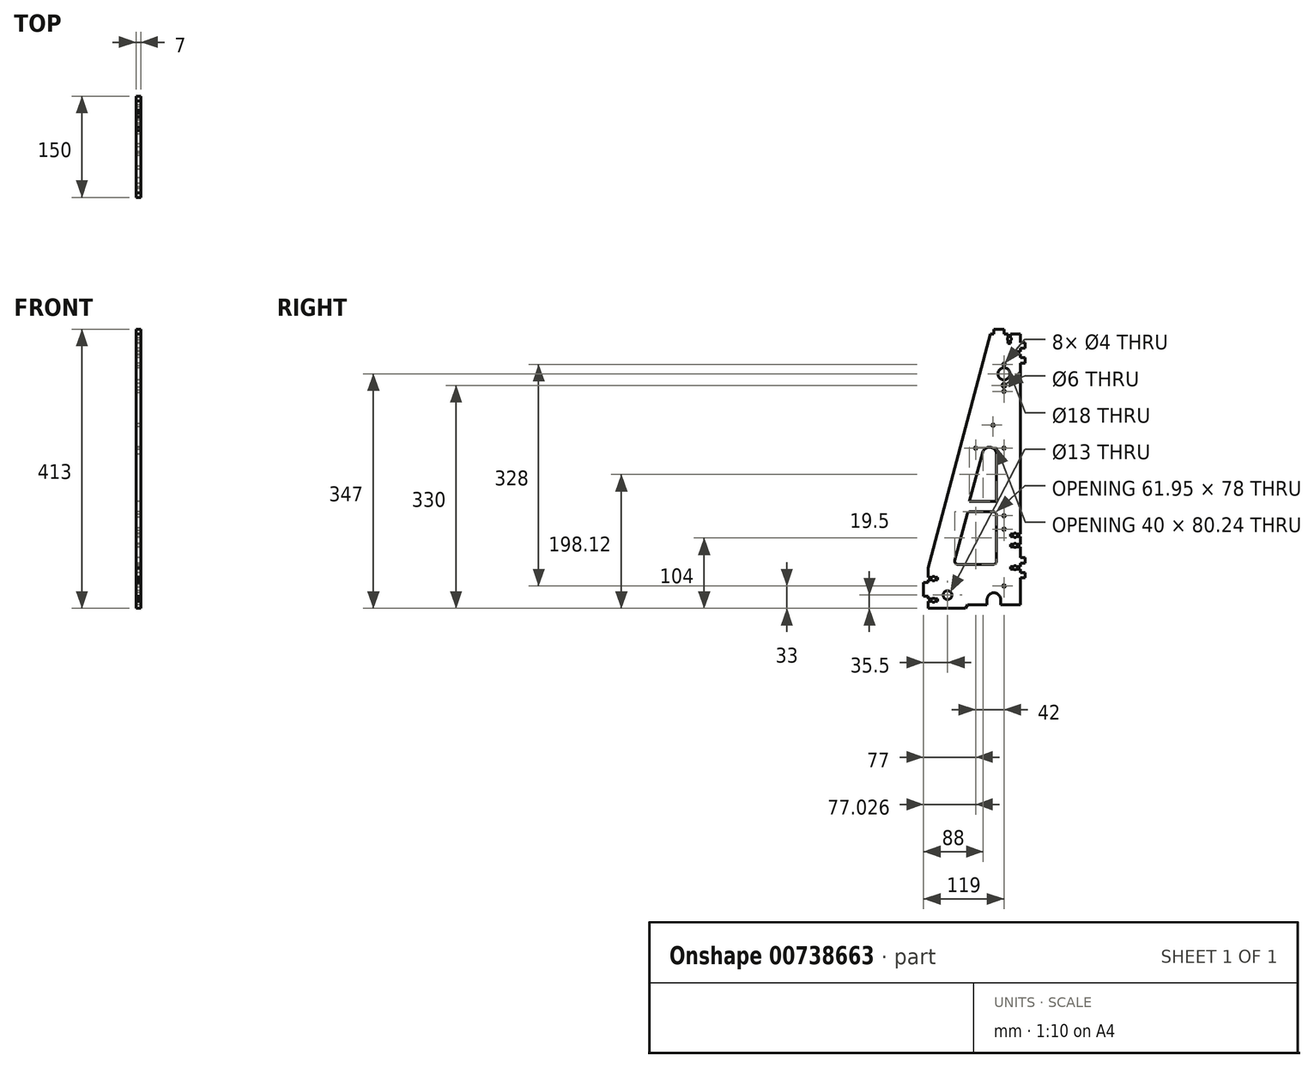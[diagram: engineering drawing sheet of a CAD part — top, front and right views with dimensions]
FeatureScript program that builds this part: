
annotation { "Feature Type Name" : "Feature", "Feature Type Description" : "" }
export const myFeature = defineFeature(function(context is Context, id is Id, definition is map)
    precondition{}
    {
        {
            var Q0;
            Q0=qCreatedBy(makeId("Right.planeOp"),FACE);
            var sketch = newSketch(context, id + "F0", { "sketchPlane" : qUnion([Q0])});
            skLineSegment(sketch, "E0", {"start": v(58, 0) * mm, "end": v(87, 0) * mm});
            skLineSegment(sketch, "E1", {"start": v(136, 0) * mm, "end": v(136, 40) * mm});
            skLineSegment(sketch, "E2", {"start": v(136, 401) * mm, "end": v(122, 401) * mm});
            skLineSegment(sketch, "E3", {"start": v(92, 401) * mm, "end": v(0, 55) * mm});
            skLineSegment(sketch, "E4", {"start": v(0, 55) * mm, "end": v(0, 41) * mm});
            skLineSegment(sketch, "E5", {"start": v(136, 55) * mm, "end": v(122, 55) * mm, "construction": true});
            skLineSegment(sketch, "E6", {"start": v(136, 88) * mm, "end": v(122, 88) * mm, "construction": true});
            skLineSegment(sketch, "E7", {"start": v(136, 103) * mm, "end": v(122, 103) * mm, "construction": true});
            skLineSegment(sketch, "E8", {"start": v(136, 373) * mm, "end": v(122, 373) * mm, "construction": true});
            skLineSegment(sketch, "E9", {"start": v(136, 53) * mm, "end": v(130, 53) * mm});
            skLineSegment(sketch, "E10", {"start": v(130, 53) * mm, "end": v(130, 52) * mm});
            skLineSegment(sketch, "E11", {"start": v(130, 52) * mm, "end": v(127, 52) * mm});
            skLineSegment(sketch, "E12", {"start": v(127, 52) * mm, "end": v(127, 53) * mm});
            skLineSegment(sketch, "E13", {"start": v(127, 53) * mm, "end": v(122, 53) * mm});
            skLineSegment(sketch, "E14", {"start": v(122, 53) * mm, "end": v(122, 55) * mm});
            skLineSegment(sketch, "E15.MirrorCS", {"start": v(122, 57) * mm, "end": v(122, 55) * mm});
            skLineSegment(sketch, "E16.MirrorCS", {"start": v(127, 57) * mm, "end": v(122, 57) * mm});
            skLineSegment(sketch, "E17.MirrorCS", {"start": v(127, 58) * mm, "end": v(127, 57) * mm});
            skLineSegment(sketch, "E18.MirrorCS", {"start": v(130, 58) * mm, "end": v(127, 58) * mm});
            skLineSegment(sketch, "E19.MirrorCS", {"start": v(130, 57) * mm, "end": v(130, 58) * mm});
            skLineSegment(sketch, "E20.MirrorCS", {"start": v(136, 57) * mm, "end": v(130, 57) * mm});
            skLineSegment(sketch, "E21", {"start": v(136, 86) * mm, "end": v(130, 86) * mm});
            skLineSegment(sketch, "E22", {"start": v(130, 86) * mm, "end": v(130, 85) * mm});
            skLineSegment(sketch, "E23", {"start": v(130, 85) * mm, "end": v(127, 85) * mm});
            skLineSegment(sketch, "E24", {"start": v(127, 85) * mm, "end": v(127, 86) * mm});
            skLineSegment(sketch, "E25", {"start": v(127, 86) * mm, "end": v(122, 86) * mm});
            skLineSegment(sketch, "E26", {"start": v(122, 86) * mm, "end": v(122, 88) * mm});
            skLineSegment(sketch, "E27.MirrorCS", {"start": v(122, 90) * mm, "end": v(122, 88) * mm});
            skLineSegment(sketch, "E28.MirrorCS", {"start": v(127, 90) * mm, "end": v(122, 90) * mm});
            skLineSegment(sketch, "E29.MirrorCS", {"start": v(127, 91) * mm, "end": v(127, 90) * mm});
            skLineSegment(sketch, "E30.MirrorCS", {"start": v(130, 91) * mm, "end": v(127, 91) * mm});
            skLineSegment(sketch, "E31.MirrorCS", {"start": v(130, 90) * mm, "end": v(130, 91) * mm});
            skLineSegment(sketch, "E32.MirrorCS", {"start": v(136, 90) * mm, "end": v(130, 90) * mm});
            skLineSegment(sketch, "E33", {"start": v(136, 101) * mm, "end": v(130, 101) * mm});
            skLineSegment(sketch, "E34", {"start": v(130, 101) * mm, "end": v(130, 100) * mm});
            skLineSegment(sketch, "E35", {"start": v(130, 100) * mm, "end": v(127, 100) * mm});
            skLineSegment(sketch, "E36", {"start": v(127, 100) * mm, "end": v(127, 101) * mm});
            skLineSegment(sketch, "E37", {"start": v(127, 101) * mm, "end": v(122, 101) * mm});
            skLineSegment(sketch, "E38", {"start": v(122, 101) * mm, "end": v(122, 103) * mm});
            skLineSegment(sketch, "E39.MirrorCS", {"start": v(122, 105) * mm, "end": v(122, 103) * mm});
            skLineSegment(sketch, "E40.MirrorCS", {"start": v(127, 105) * mm, "end": v(122, 105) * mm});
            skLineSegment(sketch, "E41.MirrorCS", {"start": v(127, 106) * mm, "end": v(127, 105) * mm});
            skLineSegment(sketch, "E42.MirrorCS", {"start": v(130, 106) * mm, "end": v(127, 106) * mm});
            skLineSegment(sketch, "E43.MirrorCS", {"start": v(130, 105) * mm, "end": v(130, 106) * mm});
            skLineSegment(sketch, "E44.MirrorCS", {"start": v(136, 105) * mm, "end": v(130, 105) * mm});
            skLineSegment(sketch, "E45", {"start": v(136, 371) * mm, "end": v(130, 371) * mm});
            skLineSegment(sketch, "E46", {"start": v(130, 371) * mm, "end": v(130, 370) * mm});
            skLineSegment(sketch, "E47", {"start": v(130, 370) * mm, "end": v(127, 370) * mm});
            skLineSegment(sketch, "E48", {"start": v(127, 370) * mm, "end": v(127, 371) * mm});
            skLineSegment(sketch, "E49", {"start": v(127, 371) * mm, "end": v(122, 371) * mm});
            skLineSegment(sketch, "E50", {"start": v(122, 371) * mm, "end": v(122, 373) * mm});
            skLineSegment(sketch, "E51.MirrorCS", {"start": v(122, 375) * mm, "end": v(122, 373) * mm});
            skLineSegment(sketch, "E52.MirrorCS", {"start": v(127, 375) * mm, "end": v(122, 375) * mm});
            skLineSegment(sketch, "E53.MirrorCS", {"start": v(127, 376) * mm, "end": v(127, 375) * mm});
            skLineSegment(sketch, "E54.MirrorCS", {"start": v(130, 376) * mm, "end": v(127, 376) * mm});
            skLineSegment(sketch, "E55.MirrorCS", {"start": v(130, 375) * mm, "end": v(130, 376) * mm});
            skLineSegment(sketch, "E56.MirrorCS", {"start": v(136, 375) * mm, "end": v(130, 375) * mm});
            skLineSegment(sketch, "E57.trimOffspring", {"start": v(136, 375) * mm, "end": v(136, 380) * mm});
            skLineSegment(sketch, "E58.trimOffspring", {"start": v(136, 105) * mm, "end": v(136, 358) * mm});
            skLineSegment(sketch, "E59.trimOffspring", {"start": v(136, 90) * mm, "end": v(136, 101) * mm});
            skLineSegment(sketch, "E60.trimOffspring", {"start": v(136, 57) * mm, "end": v(136, 62) * mm});
            skLineSegment(sketch, "E61.bottom", {"start": v(136, 48) * mm, "end": v(143, 48) * mm});
            skLineSegment(sketch, "E61.top", {"start": v(136, 40) * mm, "end": v(143, 40) * mm});
            skLineSegment(sketch, "E61.right", {"start": v(143, 48) * mm, "end": v(143, 40) * mm});
            skLineSegment(sketch, "E62.MirrorCS", {"start": v(136, 62) * mm, "end": v(143, 62) * mm});
            skLineSegment(sketch, "E63.MirrorCS", {"start": v(143, 62) * mm, "end": v(143, 70) * mm});
            skLineSegment(sketch, "E64.MirrorCS", {"start": v(136, 70) * mm, "end": v(143, 70) * mm});
            skLineSegment(sketch, "E65.trimOffspring", {"start": v(136, 70) * mm, "end": v(136, 86) * mm});
            skLineSegment(sketch, "E66.trimOffspring", {"start": v(136, 48) * mm, "end": v(136, 53) * mm});
            skLineSegment(sketch, "E67.bottom", {"start": v(136, 366) * mm, "end": v(143, 366) * mm});
            skLineSegment(sketch, "E67.top", {"start": v(136, 358) * mm, "end": v(143, 358) * mm});
            skLineSegment(sketch, "E67.right", {"start": v(143, 366) * mm, "end": v(143, 358) * mm});
            skLineSegment(sketch, "E68.trimOffspring", {"start": v(136, 366) * mm, "end": v(136, 371) * mm});
            skLineSegment(sketch, "E69.MirrorCS", {"start": v(136, 380) * mm, "end": v(143, 380) * mm});
            skLineSegment(sketch, "E70.MirrorCS", {"start": v(143, 380) * mm, "end": v(143, 388) * mm});
            skLineSegment(sketch, "E71.MirrorCS", {"start": v(136, 388) * mm, "end": v(143, 388) * mm});
            skLineSegment(sketch, "E72.trimOffspring", {"start": v(136, 388) * mm, "end": v(136, 401) * mm});
            skLineSegment(sketch, "E73", {"start": v(0, 0) * mm, "end": v(0, -5) * mm});
            skLineSegment(sketch, "E74", {"start": v(0, -5) * mm, "end": v(55, -5) * mm});
            skLineSegment(sketch, "E75", {"start": v(55, -5) * mm, "end": v(58, 0) * mm});
            skLineSegment(sketch, "E76", {"start": v(97, 0) * mm, "end": v(97, 8) * mm, "construction": true});
            skArc(sketch, "E77", {"start": v(107, 8) * mm, "mid": v(97, 18) * mm, "end": v(87, 8) * mm});
            skLineSegment(sketch, "E78", {"start": v(87, 8) * mm, "end": v(87, 0) * mm});
            skLineSegment(sketch, "E79", {"start": v(107, 8) * mm, "end": v(107, 0) * mm});
            skLineSegment(sketch, "E80.trimOffspring", {"start": v(107, 0) * mm, "end": v(136, 0) * mm});
            skLineSegment(sketch, "E81", {"start": v(0, 7) * mm, "end": v(14, 7) * mm, "construction": true});
            skLineSegment(sketch, "E82", {"start": v(0, 39) * mm, "end": v(14, 39) * mm, "construction": true});
            skLineSegment(sketch, "E83", {"start": v(0, 41) * mm, "end": v(6, 41) * mm});
            skLineSegment(sketch, "E84", {"start": v(6, 41) * mm, "end": v(6, 42) * mm});
            skLineSegment(sketch, "E85", {"start": v(6, 42) * mm, "end": v(9, 42) * mm});
            skLineSegment(sketch, "E86", {"start": v(9, 42) * mm, "end": v(9, 41) * mm});
            skLineSegment(sketch, "E87", {"start": v(9, 41) * mm, "end": v(14, 41) * mm});
            skLineSegment(sketch, "E88", {"start": v(14, 41) * mm, "end": v(14, 39) * mm});
            skLineSegment(sketch, "E89.MirrorCS", {"start": v(0, 37) * mm, "end": v(6, 37) * mm});
            skLineSegment(sketch, "E90.MirrorCS", {"start": v(6, 37) * mm, "end": v(6, 36) * mm});
            skLineSegment(sketch, "E91.MirrorCS", {"start": v(6, 36) * mm, "end": v(9, 36) * mm});
            skLineSegment(sketch, "E92.MirrorCS", {"start": v(9, 36) * mm, "end": v(9, 37) * mm});
            skLineSegment(sketch, "E93.MirrorCS", {"start": v(9, 37) * mm, "end": v(14, 37) * mm});
            skLineSegment(sketch, "E94.MirrorCS", {"start": v(14, 37) * mm, "end": v(14, 39) * mm});
            skLineSegment(sketch, "E95", {"start": v(0, 9) * mm, "end": v(6, 9) * mm});
            skLineSegment(sketch, "E96", {"start": v(6, 9) * mm, "end": v(6, 10) * mm});
            skLineSegment(sketch, "E97", {"start": v(6, 10) * mm, "end": v(9, 10) * mm});
            skLineSegment(sketch, "E98", {"start": v(9, 10) * mm, "end": v(9, 9) * mm});
            skLineSegment(sketch, "E99", {"start": v(9, 9) * mm, "end": v(14, 9) * mm});
            skLineSegment(sketch, "E100", {"start": v(14, 9) * mm, "end": v(14, 7) * mm});
            skLineSegment(sketch, "E101.MirrorCS", {"start": v(0, 5) * mm, "end": v(6, 5) * mm});
            skLineSegment(sketch, "E102.MirrorCS", {"start": v(6, 5) * mm, "end": v(6, 4) * mm});
            skLineSegment(sketch, "E103.MirrorCS", {"start": v(6, 4) * mm, "end": v(9, 4) * mm});
            skLineSegment(sketch, "E104.MirrorCS", {"start": v(9, 4) * mm, "end": v(9, 5) * mm});
            skLineSegment(sketch, "E105.MirrorCS", {"start": v(9, 5) * mm, "end": v(14, 5) * mm});
            skLineSegment(sketch, "E106.MirrorCS", {"start": v(14, 5) * mm, "end": v(14, 7) * mm});
            skLineSegment(sketch, "E107.trimOffspring", {"start": v(0, 5) * mm, "end": v(0, 0) * mm});
            skLineSegment(sketch, "E108.trimOffspring", {"start": v(0, 37) * mm, "end": v(0, 33) * mm});
            skLineSegment(sketch, "E109", {"start": v(0, 23) * mm, "end": v(-7, 23) * mm, "construction": true});
            skLineSegment(sketch, "E110", {"start": v(-7, 23) * mm, "end": v(-7, 13) * mm});
            skLineSegment(sketch, "E111", {"start": v(-7, 13) * mm, "end": v(0, 13) * mm});
            skLineSegment(sketch, "E112.MirrorCS", {"start": v(-7, 23) * mm, "end": v(-7, 33) * mm});
            skLineSegment(sketch, "E113.MirrorCS", {"start": v(-7, 33) * mm, "end": v(0, 33) * mm});
            skLineSegment(sketch, "E114.trimOffspring", {"start": v(0, 13) * mm, "end": v(0, 9) * mm});
            skCircle(sketch, "E115", {"center": v(112, 28) * mm, "radius": 2 * mm});
            skLineSegment(sketch, "E116", {"start": v(112, 28) * mm, "end": v(33, 28) * mm, "construction": true});
            skCircle(sketch, "E117", {"center": v(71, 28) * mm, "radius": 2 * mm, "construction": true});
            skCircle(sketch, "E118", {"center": v(33, 28) * mm, "radius": 2 * mm, "construction": true});
            skCircle(sketch, "E119", {"center": v(28.5, 14.5) * mm, "radius": 6.5 * mm});
            skCircle(sketch, "E120", {"center": v(112, 342) * mm, "radius": 9 * mm});
            skCircle(sketch, "E121", {"center": v(112, 325) * mm, "radius": 3 * mm});
            skLineSegment(sketch, "E122", {"start": v(112, 28) * mm, "end": v(112, 401) * mm, "construction": true});
            skCircle(sketch, "E123", {"center": v(112, 112) * mm, "radius": 2 * mm});
            skCircle(sketch, "E124", {"center": v(112, 132) * mm, "radius": 2 * mm});
            skCircle(sketch, "E125", {"center": v(112, 232) * mm, "radius": 2 * mm});
            skLineSegment(sketch, "E126", {"start": v(112, 112) * mm, "end": v(15.16, 112) * mm, "construction": true});
            skCircle(sketch, "E127", {"center": v(32, 112) * mm, "radius": 2 * mm, "construction": true});
            skLineSegment(sketch, "E128", {"start": v(112, 232) * mm, "end": v(47.06, 232) * mm, "construction": true});
            skCircle(sketch, "E129", {"center": v(70, 232) * mm, "radius": 2 * mm});
            skLineSegment(sketch, "E130", {"start": v(62.13, 138) * mm, "end": v(96, 138) * mm});
            skLineSegment(sketch, "E131", {"start": v(101, 133) * mm, "end": v(101, 65) * mm});
            skLineSegment(sketch, "E132", {"start": v(96, 60) * mm, "end": v(44.05, 60) * mm});
            skLineSegment(sketch, "E133", {"start": v(39.22, 66.28) * mm, "end": v(57.3, 134.28) * mm});
            skPoint(sketch, "E134.visualSharp", {"position": v(37.55, 60) * mm});
            skArc(sketch, "E134.filletArc", {"start": v(39.22, 66.28) * mm, "mid": v(40.08, 61.95) * mm, "end": v(44.05, 60) * mm});
            skPoint(sketch, "E135.visualSharp", {"position": v(101, 60) * mm});
            skArc(sketch, "E135.filletArc", {"start": v(96, 60) * mm, "mid": v(99.54, 61.46) * mm, "end": v(101, 65) * mm});
            skPoint(sketch, "E136.visualSharp", {"position": v(58.29, 138) * mm});
            skArc(sketch, "E136.filletArc", {"start": v(62.13, 138) * mm, "mid": v(59.08, 136.96) * mm, "end": v(57.3, 134.28) * mm});
            skPoint(sketch, "E137.visualSharp", {"position": v(101, 138) * mm});
            skArc(sketch, "E137.filletArc", {"start": v(101, 133) * mm, "mid": v(99.54, 136.54) * mm, "end": v(96, 138) * mm});
            skLineSegment(sketch, "E138", {"start": v(101, 153) * mm, "end": v(61, 153) * mm});
            skLineSegment(sketch, "E139", {"start": v(61, 153) * mm, "end": v(80.27, 225.48) * mm});
            skLineSegment(sketch, "E140", {"start": v(101, 153) * mm, "end": v(101, 223) * mm});
            skArc(sketch, "E141", {"start": v(80.27, 225.48) * mm, "mid": v(91.71, 233.24) * mm, "end": v(101, 223) * mm});
            skLineSegment(sketch, "E142", {"start": v(70.02, 60) * mm, "end": v(90.46, 222.77) * mm, "construction": true});
            skLineSegment(sketch, "E143", {"start": v(90.46, 222.77) * mm, "end": v(95.88, 265.98) * mm, "construction": true});
            skCircle(sketch, "E144", {"center": v(95.88, 265.98) * mm, "radius": 2 * mm});
            skLineSegment(sketch, "E145", {"start": v(97, 401) * mm, "end": v(97, 408) * mm});
            skLineSegment(sketch, "E146", {"start": v(97, 408) * mm, "end": v(112, 408) * mm});
            skLineSegment(sketch, "E147", {"start": v(112, 408) * mm, "end": v(112, 401) * mm});
            skLineSegment(sketch, "E148.trimOffspring", {"start": v(97, 401) * mm, "end": v(92, 401) * mm});
            skLineSegment(sketch, "E149", {"start": v(120, 401) * mm, "end": v(120, 387) * mm, "construction": true});
            skLineSegment(sketch, "E150", {"start": v(122, 401) * mm, "end": v(122, 395) * mm});
            skLineSegment(sketch, "E151", {"start": v(122, 395) * mm, "end": v(123, 395) * mm});
            skLineSegment(sketch, "E152", {"start": v(123, 395) * mm, "end": v(123, 392) * mm});
            skLineSegment(sketch, "E153", {"start": v(123, 392) * mm, "end": v(122, 392) * mm});
            skLineSegment(sketch, "E154", {"start": v(122, 392) * mm, "end": v(122, 387) * mm});
            skLineSegment(sketch, "E155", {"start": v(122, 387) * mm, "end": v(120, 387) * mm});
            skLineSegment(sketch, "E156.MirrorCS", {"start": v(118, 401) * mm, "end": v(118, 395) * mm});
            skLineSegment(sketch, "E157.MirrorCS", {"start": v(118, 395) * mm, "end": v(117, 395) * mm});
            skLineSegment(sketch, "E158.MirrorCS", {"start": v(117, 395) * mm, "end": v(117, 392) * mm});
            skLineSegment(sketch, "E159.MirrorCS", {"start": v(117, 392) * mm, "end": v(118, 392) * mm});
            skLineSegment(sketch, "E160.MirrorCS", {"start": v(118, 392) * mm, "end": v(118, 387) * mm});
            skLineSegment(sketch, "E161.MirrorCS", {"start": v(118, 387) * mm, "end": v(120, 387) * mm});
            skLineSegment(sketch, "E162.trimOffspring", {"start": v(118, 401) * mm, "end": v(112, 401) * mm});
            skCircle(sketch, "E163", {"center": v(112, 356) * mm, "radius": 2 * mm});
            skCircle(sketch, "E164", {"center": v(112, 316) * mm, "radius": 2 * mm});
            skSolve(sketch);
        }
        {
            var Q0;
            Q0 = qSketchRegion(id + "F0", true);
            extrude(context, id + "F1", {"entities" : qUnion([Q0]), "depth" : 7 * mm, "offsetDistance" : 25 * mm});
        }
    });
